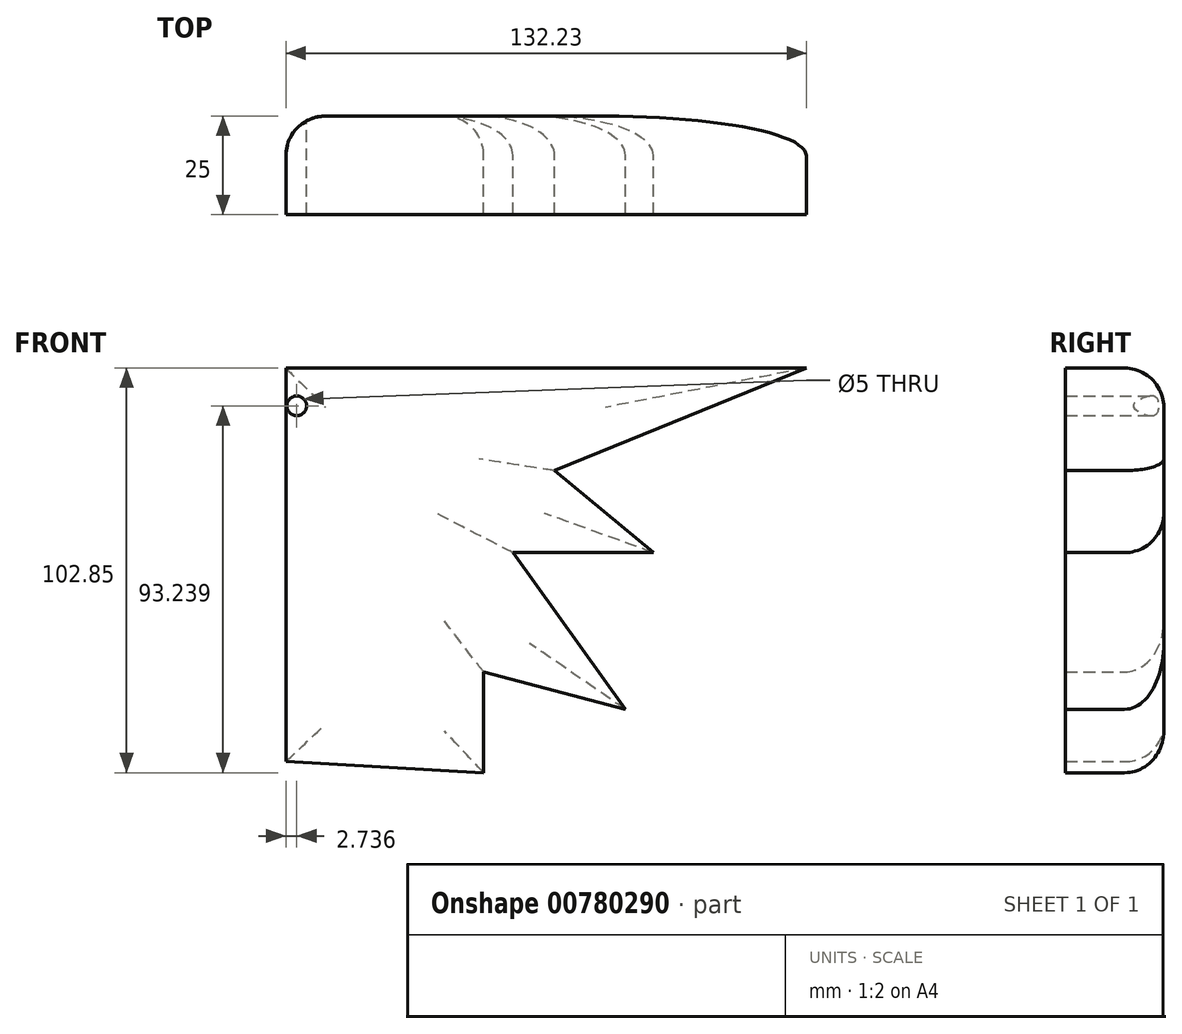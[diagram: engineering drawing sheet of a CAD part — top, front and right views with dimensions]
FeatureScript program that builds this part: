
annotation { "Feature Type Name" : "Feature", "Feature Type Description" : "" }
export const myFeature = defineFeature(function(context is Context, id is Id, definition is map)
    precondition{}
    {
        {
            var Q0;
            Q0=qCreatedBy(makeId("Front.planeOp"),FACE);
            var sketch = newSketch(context, id + "F0", { "sketchPlane" : qUnion([Q0])});
            skLineSegment(sketch, "E0", {"start": v(-83.13, 68.08) * mm, "end": v(-83.13, -31.92) * mm});
            skLineSegment(sketch, "E1", {"start": v(-83.13, 68.08) * mm, "end": v(49.1, 68.08) * mm});
            skLineSegment(sketch, "E2", {"start": v(49.1, 68.08) * mm, "end": v(-14.88, 42) * mm});
            skLineSegment(sketch, "E3", {"start": v(-14.88, 42) * mm, "end": v(10.24, 21.16) * mm});
            skLineSegment(sketch, "E4", {"start": v(10.24, 21.16) * mm, "end": v(-25.78, 21.16) * mm});
            skLineSegment(sketch, "E5", {"start": v(-25.78, 21.63) * mm, "end": v(3.13, -18.65) * mm});
            skLineSegment(sketch, "E6", {"start": v(3.13, -18.65) * mm, "end": v(-32.9, -9.18) * mm});
            skLineSegment(sketch, "E7", {"start": v(-32.9, -9.18) * mm, "end": v(-32.9, -34.77) * mm});
            skLineSegment(sketch, "E8", {"start": v(-32.9, -34.77) * mm, "end": v(-83.13, -31.92) * mm});
            skSolve(sketch);
        }
        {
            var Q0;
            Q0 = qSketchRegion(id + "F0", true);
            extrude(context, id + "F1", {"entities" : qUnion([Q0]), "depth" : 25 * mm, "offsetDistance" : 25 * mm});
        }
        {
            var Q0;
            Q0=qCreatedBy(makeId("Front.planeOp"),FACE);
            var sketch = newSketch(context, id + "F2", { "sketchPlane" : qUnion([Q0])});
            skCircle(sketch, "E9", {"center": v(-80.4, 58.47) * mm, "radius": 2.5 * mm});
            skSolve(sketch);
        }
        {
            var Q0;
            Q0 = qSketchRegion(id + "F2", true);
            extrude(context, id + "F3", {"entities" : qUnion([Q0]), "operationType" : NewBodyOperationType.REMOVE, "depth" : 46.9 * mm, "offsetDistance" : 25 * mm});
        }
        {
            var Q0;
            Q0=makeQuery(id+"F1.opExtrude","CAP_EDGE",EDGE,{"disambiguationData":[OSD([sQuery(id+"F0.wireOp",EDGE,"E0")])],"isStart":true});
            var Q1;
            Q1=makeQuery(id+"F1.opExtrude","CAP_EDGE",EDGE,{"disambiguationData":[OSD([sQuery(id+"F0.wireOp",EDGE,"E1")])],"isStart":true});
            var Q2;
            Q2=makeQuery(id+"F1.opExtrude","CAP_EDGE",EDGE,{"disambiguationData":[OSD([sQuery(id+"F0.wireOp",EDGE,"E7")])],"isStart":true});
            var Q3;
            Q3=makeQuery(id+"F1.opExtrude","CAP_EDGE",EDGE,{"disambiguationData":[OSD([sQuery(id+"F0.wireOp",EDGE,"E8")])],"isStart":true});
            var Q4;
            Q4=makeQuery(id+"F1.opExtrude","CAP_EDGE",EDGE,{"disambiguationData":[OSD([sQuery(id+"F0.wireOp",EDGE,"E6")])],"isStart":true});
            var Q5;
            Q5=makeQuery(id+"F1.opExtrude","CAP_EDGE",EDGE,{"disambiguationData":[OSD([sQuery(id+"F0.wireOp",EDGE,"E5")])],"isStart":true});
            var Q6;
            Q6=makeQuery(id+"F1.opExtrude","CAP_EDGE",EDGE,{"disambiguationData":[OSD([sQuery(id+"F0.wireOp",EDGE,"E4")])],"isStart":true});
            var Q7;
            Q7=makeQuery(id+"F1.opExtrude","CAP_EDGE",EDGE,{"disambiguationData":[OSD([sQuery(id+"F0.wireOp",EDGE,"E3")])],"isStart":true});
            var Q8;
            Q8=makeQuery(id+"F1.opExtrude","CAP_EDGE",EDGE,{"disambiguationData":[OSD([sQuery(id+"F0.wireOp",EDGE,"E2")])],"isStart":true});
            fillet(context, id + "F4", {"entities" : qUnion([Q0, Q1, Q2, Q3, Q4, Q5, Q6, Q7, Q8]), "radius" : 10 * mm, "tangentPropagation" : true, "allowEdgeOverflow" : false});
        }
    });
